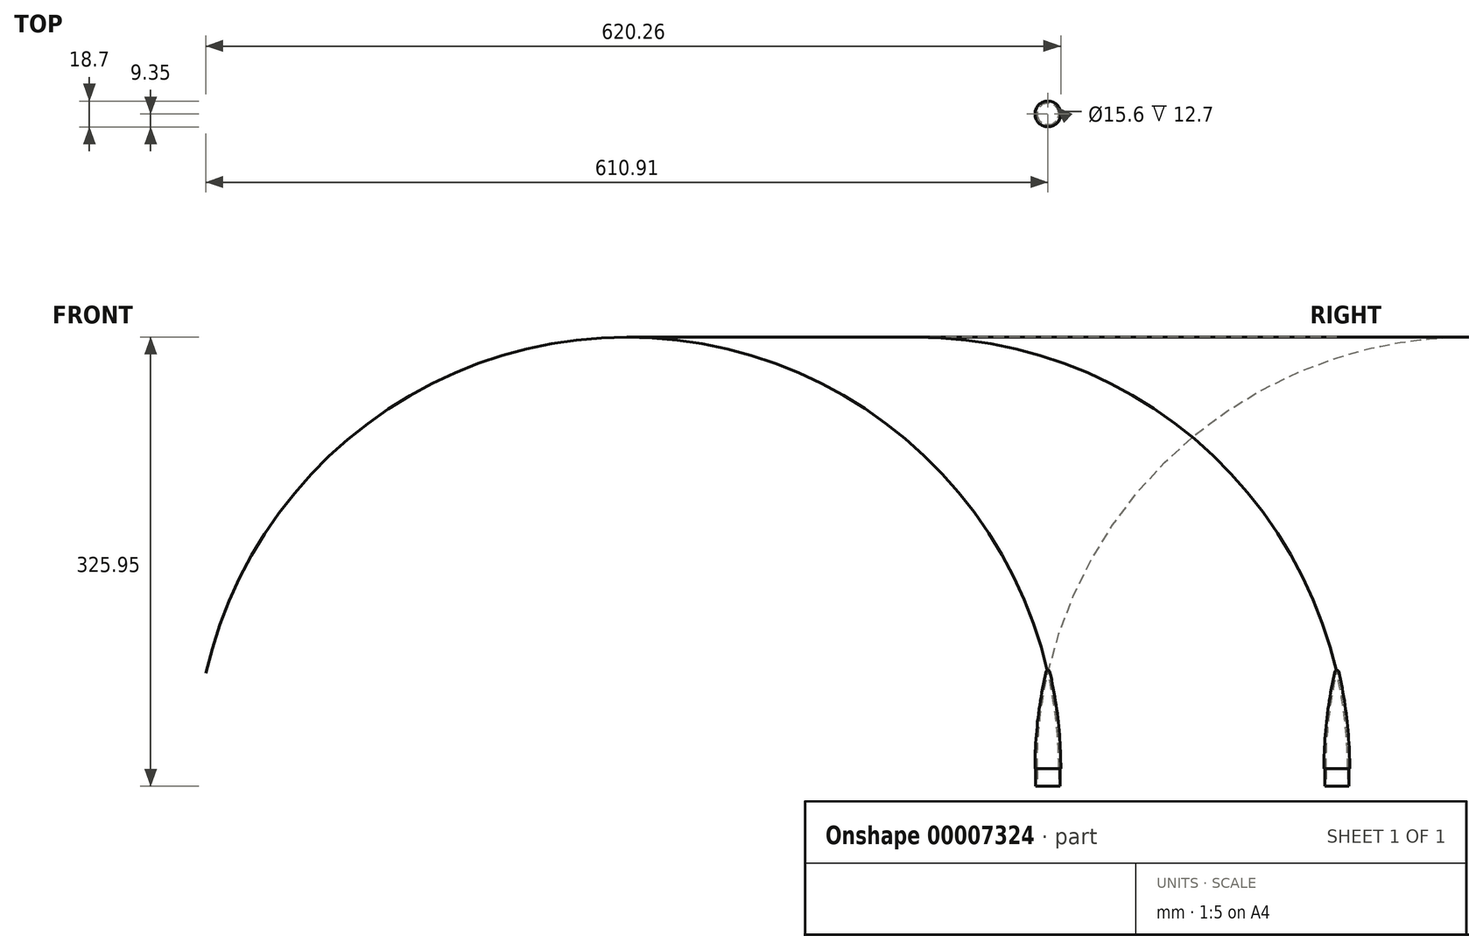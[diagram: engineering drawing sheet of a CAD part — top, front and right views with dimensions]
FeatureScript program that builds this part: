
annotation { "Feature Type Name" : "Feature", "Feature Type Description" : "" }
export const myFeature = defineFeature(function(context is Context, id is Id, definition is map)
    precondition{}
    {
        {
            var Q0;
            Q0=qCreatedBy(makeId("Front.planeOp"),FACE);
            var sketch = newSketch(context, id + "F0", { "sketchPlane" : qUnion([Q0])});
            skLineSegment(sketch, "E0", {"start": v(0, 0) * mm, "end": v(0, 84.33) * mm});
            skLineSegment(sketch, "E1", {"start": v(0, 0) * mm, "end": v(8.84, 0) * mm});
            skLineSegment(sketch, "E2", {"start": v(8.84, 0) * mm, "end": v(8.84, 12.7) * mm});
            skLineSegment(sketch, "E3", {"start": v(8.84, 12.7) * mm, "end": v(9.35, 12.7) * mm});
            skLineSegment(sketch, "E4", {"start": v(8.84, 12.7) * mm, "end": v(0, 12.7) * mm, "construction": true});
            skArc(sketch, "E5", {"start": v(1.34, 83.26) * mm, "mid": v(0.85, 84.03) * mm, "end": v(0, 84.33) * mm});
            skLineSegment(sketch, "E6", {"start": v(9.35, 12.7) * mm, "end": v(9.35, 0) * mm});
            skLineSegment(sketch, "E7", {"start": v(9.35, 0) * mm, "end": v(8.84, 0) * mm});
            skArc(sketch, "E8", {"start": v(9.35, 12.7) * mm, "mid": v(7.34, 48.2) * mm, "end": v(1.34, 83.26) * mm});
            skLineSegment(sketch, "E9", {"start": v(7.8, 0) * mm, "end": v(7.8, 12.7) * mm});
            skArc(sketch, "E10", {"start": v(7.8, 12.7) * mm, "mid": v(5.84, 47.65) * mm, "end": v(0, 82.16) * mm});
            skSolve(sketch);
        }
        {
            var Q0;
            {var subQ3=sQuery(id+"F0.wireOp",EDGE,"E2");Q0=makeQuery(id+"F0.imprint","IMPRINT",FACE,{"disambiguationData":[TD([[makeQuery(id+"F0.imprint","IMPRINT",EDGE,{"derivedFrom":subQ3}),1.0]])]});}
            var Q1;
            Q1=sQuery(id+"F0.wireOp",EDGE,"E0");
            revolve(context, id + "F1", {"entities" : qUnion([Q0]), "axis" : qUnion([Q1]), "revolveType" : RevolveType.FULL});
        }
    });
